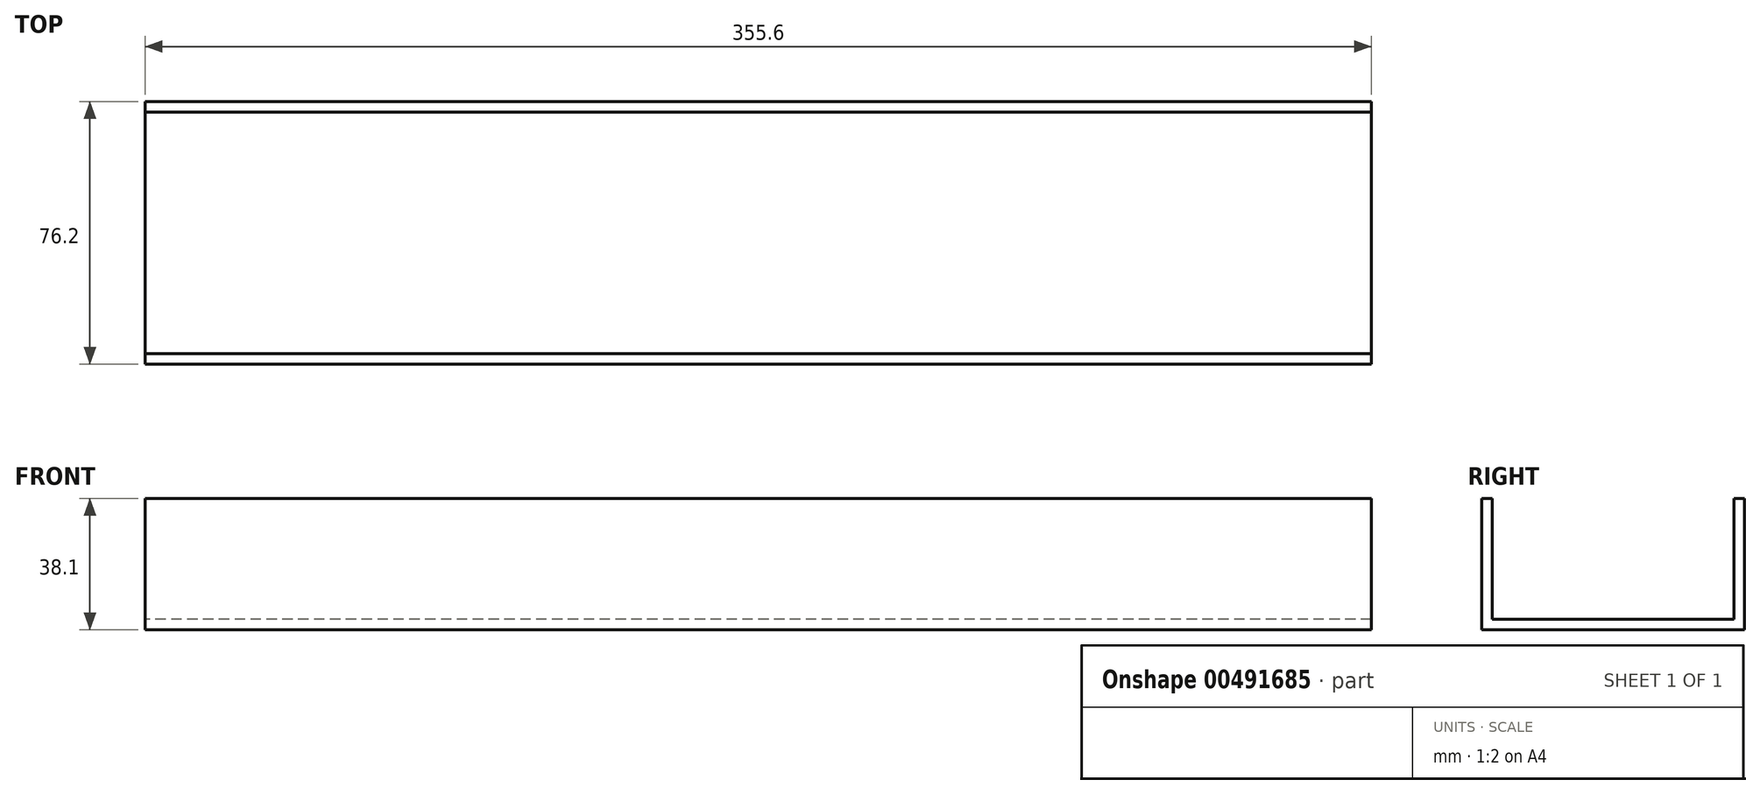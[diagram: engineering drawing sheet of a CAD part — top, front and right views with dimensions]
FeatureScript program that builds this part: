
annotation { "Feature Type Name" : "Feature", "Feature Type Description" : "" }
export const myFeature = defineFeature(function(context is Context, id is Id, definition is map)
    precondition{}
    {
        {
            var Q0;
            Q0=qCreatedBy(makeId("Right.planeOp"),FACE);
            var sketch = newSketch(context, id + "F0", { "sketchPlane" : qUnion([Q0])});
            skLineSegment(sketch, "E0", {"start": v(-22.02, 38.1) * mm, "end": v(-22.02, 0) * mm});
            skLineSegment(sketch, "E1", {"start": v(-22.02, 0) * mm, "end": v(54.18, 0) * mm});
            skLineSegment(sketch, "E2", {"start": v(54.18, 0) * mm, "end": v(54.18, 38.1) * mm});
            skLineSegment(sketch, "E3", {"start": v(54.18, 38.1) * mm, "end": v(51.18, 38.1) * mm});
            skLineSegment(sketch, "E4", {"start": v(51.18, 38.1) * mm, "end": v(51.18, 3) * mm});
            skLineSegment(sketch, "E5", {"start": v(51.18, 3) * mm, "end": v(-19.02, 3) * mm});
            skLineSegment(sketch, "E6", {"start": v(-19.02, 3) * mm, "end": v(-19.02, 38.1) * mm});
            skLineSegment(sketch, "E7", {"start": v(-19.02, 38.1) * mm, "end": v(-22.02, 38.1) * mm});
            skSolve(sketch);
        }
        {
            var Q0;
            Q0=makeQuery(id+"F0.imprint","IMPRINT",FACE,{"disambiguationData":[TD([[makeQuery(id+"F0.imprint","IMPRINT",EDGE,{"derivedFrom":sQuery(id+"F0.wireOp",EDGE,"E0")}),1.0]])]});
            extrude(context, id + "F1", {"entities" : qUnion([Q0]), "depth" : 355.6 * mm});
        }
    });
